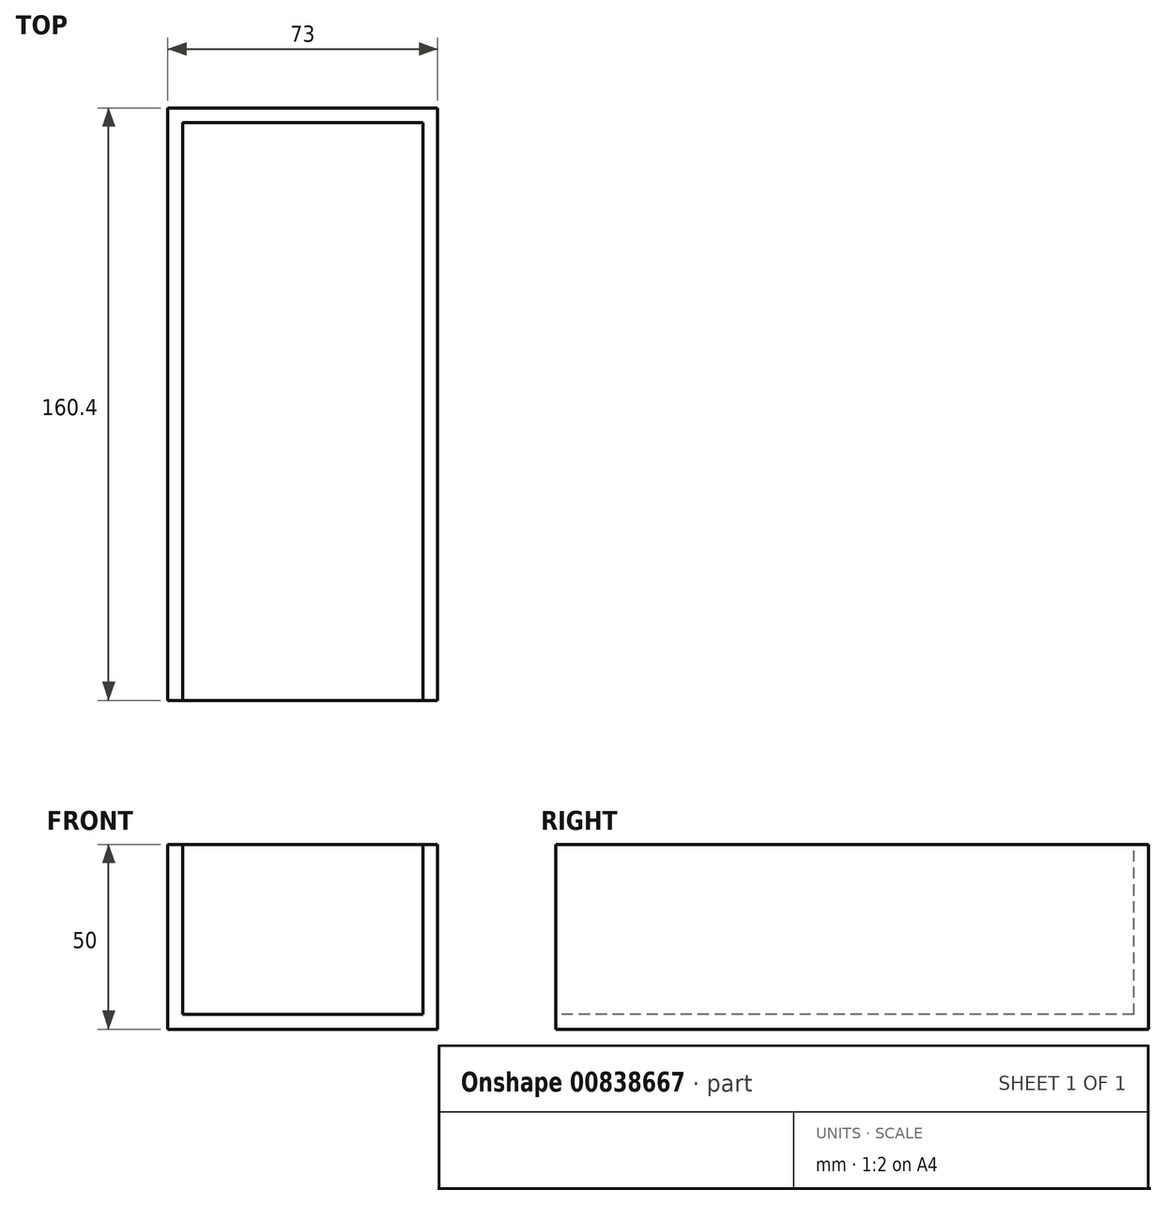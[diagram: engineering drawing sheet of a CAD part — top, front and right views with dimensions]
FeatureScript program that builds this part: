
annotation { "Feature Type Name" : "Feature", "Feature Type Description" : "" }
export const myFeature = defineFeature(function(context is Context, id is Id, definition is map)
    precondition{}
    {
        {
            var Q0;
            Q0=qCreatedBy(makeId("Front.planeOp"),FACE);
            var sketch = newSketch(context, id + "F0", { "sketchPlane" : qUnion([Q0])});
            skLineSegment(sketch, "E0.bottom", {"start": v(0, 0) * mm, "end": v(73, 0) * mm});
            skLineSegment(sketch, "E0.top", {"start": v(0, 50) * mm, "end": v(73, 50) * mm});
            skLineSegment(sketch, "E0.left", {"start": v(0, 0) * mm, "end": v(0, 50) * mm});
            skLineSegment(sketch, "E0.right", {"start": v(73, 0) * mm, "end": v(73, 50) * mm});
            skSolve(sketch);
        }
        {
            var Q0;
            Q0=makeQuery(id+"F0.imprint","IMPRINT",FACE,{"disambiguationData":[TD([[makeQuery(id+"F0.imprint","IMPRINT",EDGE,{"derivedFrom":sQuery(id+"F0.wireOp",EDGE,"E0.bottom")}),1.0]])]});
            extrude(context, id + "F1", {"entities" : qUnion([Q0]), "depth" : 160.4 * mm, "offsetDistance" : 25 * mm});
        }
        {
            var Q0;
            Q0=makeQuery(id+"F1.opExtrude","SWEPT_FACE",FACE,{"disambiguationData":[OSD([sQuery(id+"F0.wireOp",EDGE,"E0.top")])]});
            var sketch = newSketch(context, id + "F2", { "sketchPlane" : qUnion([Q0])});
            skLineSegment(sketch, "E1.bottom", {"start": v(4, -4) * mm, "end": v(69, -4) * mm});
            skLineSegment(sketch, "E1.top", {"start": v(4, -160.4) * mm, "end": v(69, -160.4) * mm});
            skLineSegment(sketch, "E1.left", {"start": v(4, -4) * mm, "end": v(4, -160.4) * mm});
            skLineSegment(sketch, "E1.right", {"start": v(69, -4) * mm, "end": v(69, -160.4) * mm});
            skSolve(sketch);
        }
        {
            var Q0;
            Q0 = qSketchRegion(id + "F2", true);
            extrude(context, id + "F3", {"entities" : qUnion([Q0]), "operationType" : NewBodyOperationType.REMOVE, "oppositeDirection" : true, "depth" : 46 * mm, "offsetDistance" : 25 * mm});
        }
    });
